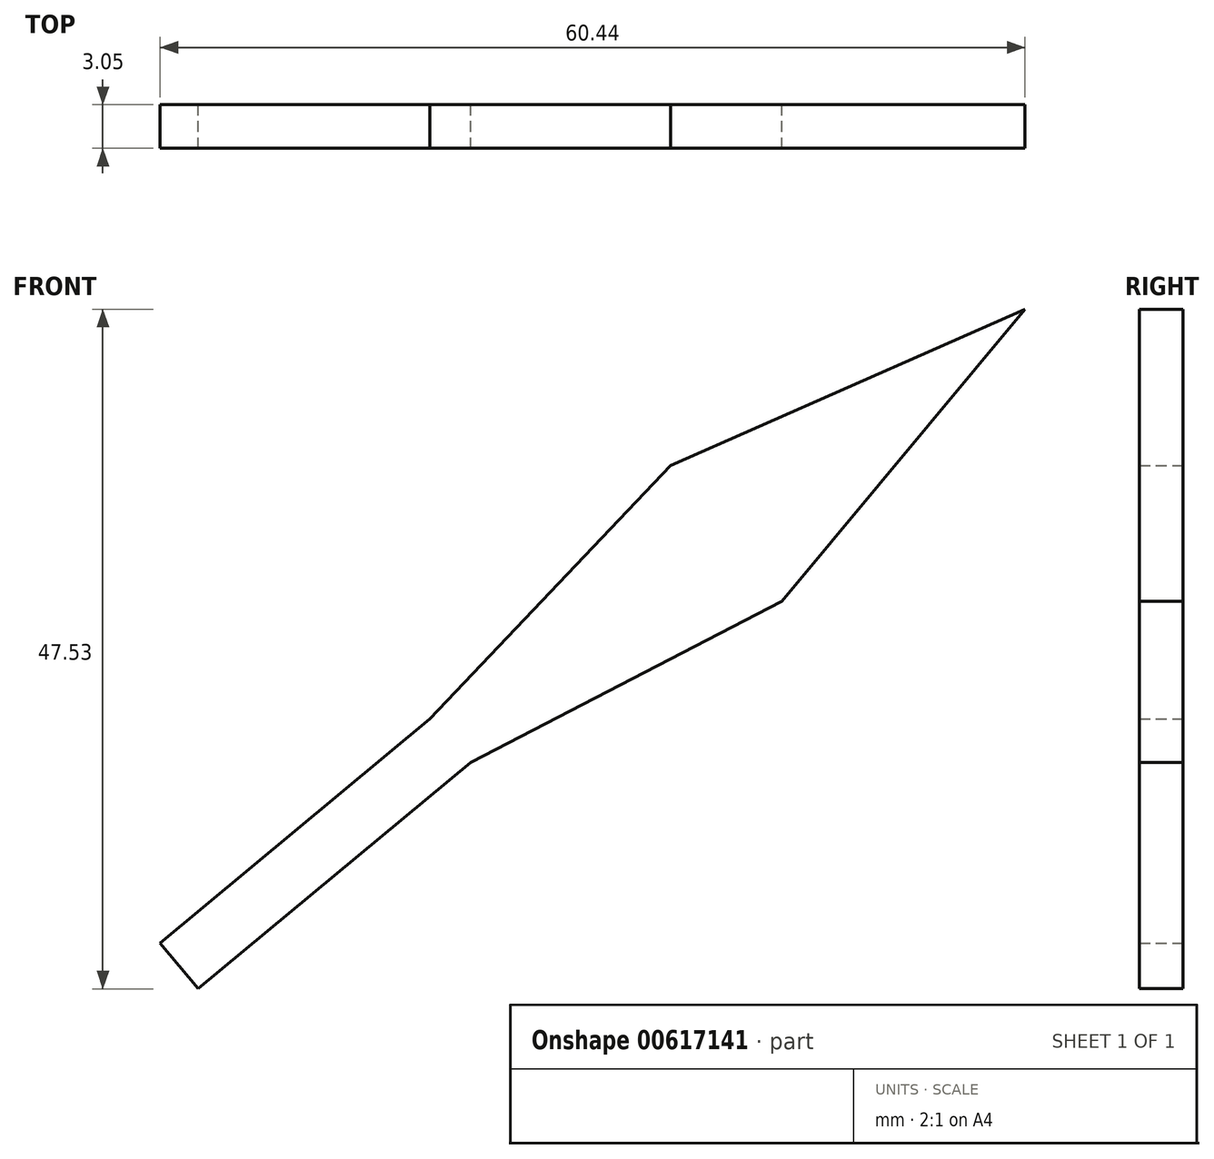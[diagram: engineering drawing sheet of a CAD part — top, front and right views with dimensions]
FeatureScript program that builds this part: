
annotation { "Feature Type Name" : "Feature", "Feature Type Description" : "" }
export const myFeature = defineFeature(function(context is Context, id is Id, definition is map)
    precondition{}
    {
        {
            var Q0;
            Q0=qCreatedBy(makeId("Front.planeOp"),FACE);
            var sketch = newSketch(context, id + "F0", { "sketchPlane" : qUnion([Q0])});
            skLineSegment(sketch, "E0", {"start": v(0, 0) * mm, "end": v(-18.85, -15.69) * mm});
            skLineSegment(sketch, "E1", {"start": v(-18.85, -15.69) * mm, "end": v(-16.19, -18.89) * mm});
            skLineSegment(sketch, "E2", {"start": v(-16.19, -18.89) * mm, "end": v(2.85, -3.04) * mm});
            skLineSegment(sketch, "E3", {"start": v(2.85, -3.04) * mm, "end": v(0, 0) * mm});
            skLineSegment(sketch, "E4", {"start": v(2.85, -3.04) * mm, "end": v(24.6, 8.2) * mm});
            skLineSegment(sketch, "E5", {"start": v(24.6, 8.2) * mm, "end": v(41.59, 28.64) * mm});
            skLineSegment(sketch, "E6", {"start": v(41.59, 28.64) * mm, "end": v(16.84, 17.7) * mm});
            skLineSegment(sketch, "E7", {"start": v(16.84, 17.7) * mm, "end": v(0, 0) * mm});
            skSolve(sketch);
        }
        {
            var Q0;
            Q0=makeQuery(id+"F0.imprint","IMPRINT",FACE,{"disambiguationData":[TD([[makeQuery(id+"F0.imprint","IMPRINT",EDGE,{"derivedFrom":sQuery(id+"F0.wireOp",EDGE,"E3")}),-1.0]])]});
            var Q1;
            Q1=makeQuery(id+"F0.imprint","IMPRINT",FACE,{"disambiguationData":[TD([[makeQuery(id+"F0.imprint","IMPRINT",EDGE,{"derivedFrom":sQuery(id+"F0.wireOp",EDGE,"E0")}),1.0]])]});
            extrude(context, id + "F1", {"entities" : qUnion([Q0, Q1]), "depth" : 3.05 * mm, "offsetDistance" : 25.4 * mm});
        }
    });
